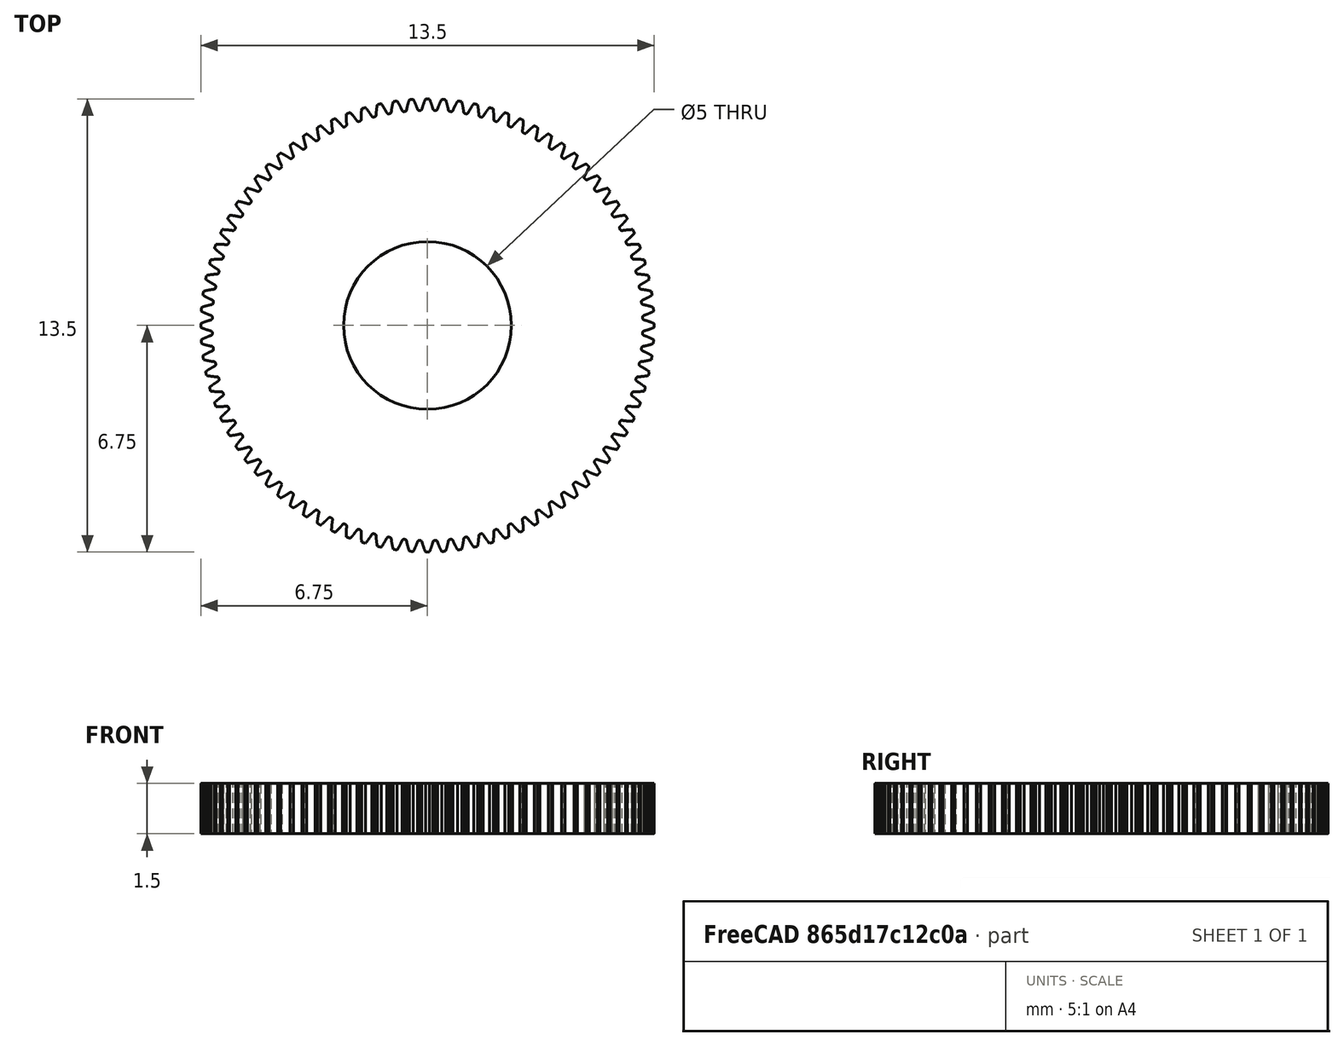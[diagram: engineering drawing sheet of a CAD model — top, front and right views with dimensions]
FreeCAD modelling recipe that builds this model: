
FCSTD DOCUMENT  (FreeCAD 0.18.1R)
Label: Couronne_M015_88
License: All rights reserved
LicenseURL: http://en.wikipedia.org/wiki/All_rights_reserved
objects: Part::Part2DObjectPython×1, PartDesign::Pad×1, Sketcher::SketchObject×1, PartDesign::Pocket×1, PartDesign::Body×1
note: 7 computed .brp shape members not serialized (recipe doc carries the construction recipe); baked Part::Feature solids carry a one-line shape summary decoded from their .brp

FEATURE [Part::Part2DObjectPython] InvoluteGear  # Draft 2D object (typed FeaturePython)
  ExternalGear = true
  HighPrecision = true
  Modules = 0.15
  NumberOfTeeth = 88
  PressureAngle = 20
FEATURE [PartDesign::Pad] Pad
  Length = 1.5
  Length2 = 100
  Profile = -> InvoluteGear
  Type = 0
FEATURE [Sketcher::SketchObject] Sketch
  MapMode = 2
  sketch-geometry (1):
    g0: Circle CenterX=0 CenterY=0 CenterZ=0 NormalX=0 NormalY=0 NormalZ=1 AngleXU=0 Radius=2.5
  constraints (2):
    c: Coincident(g0,g-1)
    c: Radius(g0) = 2.5
FEATURE [PartDesign::Pocket] Pocket
  BaseFeature = -> Pad
  Length = 5
  Length2 = 100
  Profile = -> Sketch
  Reversed = true
  Type = 1
FEATURE [PartDesign::Body] Body
  Group = -> [InvoluteGear,Pad,Sketch,Pocket]
  Origin = -> Origin
  Tip = -> Pocket
